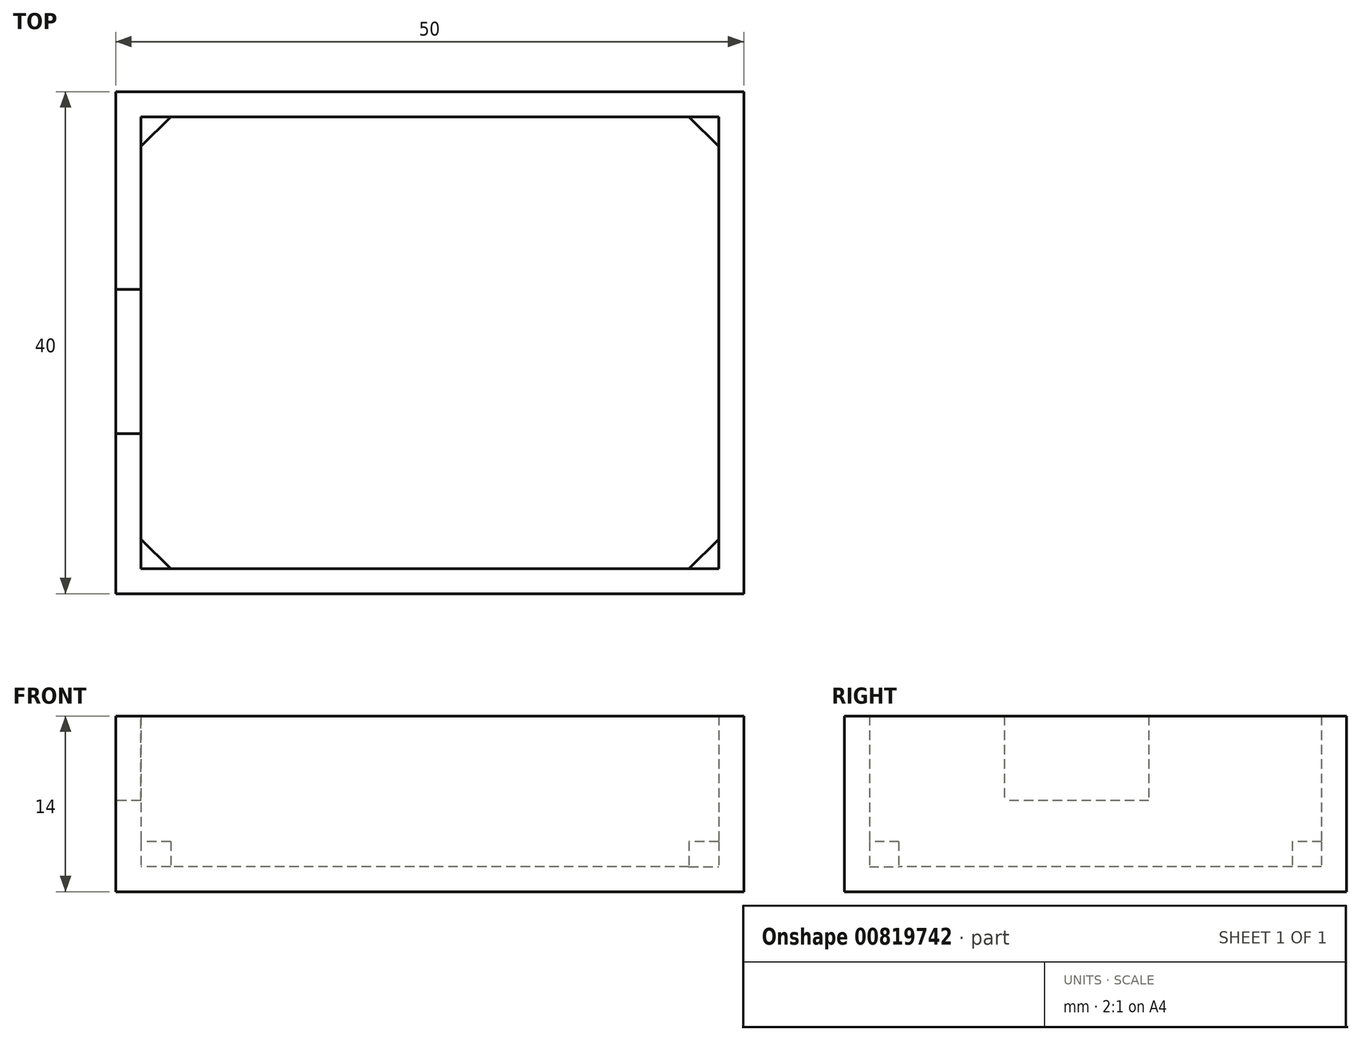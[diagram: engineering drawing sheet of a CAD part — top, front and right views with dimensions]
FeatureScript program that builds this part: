
annotation { "Feature Type Name" : "Feature", "Feature Type Description" : "" }
export const myFeature = defineFeature(function(context is Context, id is Id, definition is map)
    precondition{}
    {
        {
            var Q0;
            Q0=qCreatedBy(makeId("Top.planeOp"),FACE);
            var sketch = newSketch(context, id + "F0", { "sketchPlane" : qUnion([Q0])});
            skLineSegment(sketch, "E0.bottom", {"start": v(29.02, 30.23) * mm, "end": v(-16.98, 30.23) * mm});
            skLineSegment(sketch, "E0.top", {"start": v(29.02, -5.77) * mm, "end": v(-16.98, -5.77) * mm});
            skLineSegment(sketch, "E0.left", {"start": v(29.02, 30.23) * mm, "end": v(29.02, -5.77) * mm});
            skLineSegment(sketch, "E0.right", {"start": v(-16.98, 30.23) * mm, "end": v(-16.98, -5.77) * mm});
            skLineSegment(sketch, "E1.0", {"start": v(31.02, 32.23) * mm, "end": v(-18.98, 32.23) * mm});
            skLineSegment(sketch, "E1.1", {"start": v(31.02, 32.23) * mm, "end": v(31.02, -7.77) * mm});
            skLineSegment(sketch, "E1.2", {"start": v(31.02, -7.77) * mm, "end": v(-18.98, -7.77) * mm});
            skLineSegment(sketch, "E1.3", {"start": v(-18.98, 32.23) * mm, "end": v(-18.98, -7.77) * mm});
            skLineSegment(sketch, "E2", {"start": v(-14.6, 30.23) * mm, "end": v(-16.98, 27.88) * mm});
            skLineSegment(sketch, "E3", {"start": v(6.02, 32.23) * mm, "end": v(6.02, -7.77) * mm, "construction": true});
            skLineSegment(sketch, "E4", {"start": v(31.02, 12.23) * mm, "end": v(-18.98, 12.23) * mm, "construction": true});
            skLineSegment(sketch, "E5.MirrorCS", {"start": v(26.65, 30.23) * mm, "end": v(29.02, 27.88) * mm});
            skLineSegment(sketch, "E6.MirrorCS", {"start": v(26.65, -5.77) * mm, "end": v(29.02, -3.43) * mm});
            skLineSegment(sketch, "E7.MirrorCS", {"start": v(-14.6, -5.77) * mm, "end": v(-16.98, -3.43) * mm});
            skSolve(sketch);
        }
        {
            var Q0;
            {var subQ0=sQuery(id+"F0.wireOp",EDGE,"E2");Q0=makeQuery(id+"F0.imprint","IMPRINT",FACE,{"disambiguationData":[TD([[makeQuery(id+"F0.imprint","IMPRINT",EDGE,{"derivedFrom":subQ0}),1.0]])]});}
            extrude(context, id + "F1", {"entities" : qUnion([Q0]), "depth" : 2 * mm, "offsetDistance" : 25 * mm});
        }
        {
            var Q0;
            {var subQ3=sQuery(id+"F0.wireOp",EDGE,"E7.MirrorCS");Q0=makeQuery(id+"F0.imprint","IMPRINT",FACE,{"disambiguationData":[TD([[makeQuery(id+"F0.imprint","IMPRINT",EDGE,{"derivedFrom":subQ3}),1.0]])]});}
            var Q1;
            {var subQ3=sQuery(id+"F0.wireOp",EDGE,"E6.MirrorCS");Q1=makeQuery(id+"F0.imprint","IMPRINT",FACE,{"disambiguationData":[TD([[makeQuery(id+"F0.imprint","IMPRINT",EDGE,{"derivedFrom":subQ3}),-1.0]])]});}
            var Q2;
            {var subQ3=sQuery(id+"F0.wireOp",EDGE,"E2");Q2=makeQuery(id+"F0.imprint","IMPRINT",FACE,{"disambiguationData":[TD([[makeQuery(id+"F0.imprint","IMPRINT",EDGE,{"derivedFrom":subQ3}),-1.0]])]});}
            var Q3;
            {var subQ3=sQuery(id+"F0.wireOp",EDGE,"E5.MirrorCS");Q3=makeQuery(id+"F0.imprint","IMPRINT",FACE,{"disambiguationData":[TD([[makeQuery(id+"F0.imprint","IMPRINT",EDGE,{"derivedFrom":subQ3}),1.0]])]});}
            extrude(context, id + "F2", {"entities" : qUnion([Q0, Q1, Q2, Q3]), "operationType" : NewBodyOperationType.ADD, "depth" : 4 * mm, "offsetDistance" : 25 * mm});
        }
        {
            var Q0;
            Q0=makeQuery(id+"F0.imprint","IMPRINT",FACE,{"disambiguationData":[TD([[makeQuery(id+"F0.imprint","IMPRINT",EDGE,{"derivedFrom":sQuery(id+"F0.wireOp",EDGE,"E1.0")}),1.0]])]});
            extrude(context, id + "F3", {"entities" : qUnion([Q0]), "operationType" : NewBodyOperationType.ADD, "depth" : 14 * mm, "offsetDistance" : 25 * mm});
        }
        {
            var Q0;
            Q0=makeQuery(id+"F3.opExtrude","SWEPT_FACE",FACE,{"disambiguationData":[OSD([sQuery(id+"F0.wireOp",EDGE,"E1.3")])]});
            var sketch = newSketch(context, id + "F4", { "sketchPlane" : qUnion([Q0])});
            skLineSegment(sketch, "E8.bottom", {"start": v(-16.48, 15) * mm, "end": v(-4.98, 15) * mm});
            skLineSegment(sketch, "E8.top", {"start": v(-16.48, 7.25) * mm, "end": v(-4.98, 7.25) * mm});
            skLineSegment(sketch, "E8.left", {"start": v(-16.48, 15) * mm, "end": v(-16.48, 7.25) * mm});
            skLineSegment(sketch, "E8.right", {"start": v(-4.98, 15) * mm, "end": v(-4.98, 7.25) * mm});
            skSolve(sketch);
        }
        {
            var Q0;
            {var subQ0=sQuery(id+"F4.wireOp",EDGE,"E8.top");Q0=makeQuery(id+"F4.imprint","IMPRINT",FACE,{"disambiguationData":[TD([[makeQuery(id+"F4.imprint","IMPRINT",EDGE,{"derivedFrom":subQ0}),1.0]])]});}
            extrude(context, id + "F5", {"entities" : qUnion([Q0]), "operationType" : NewBodyOperationType.REMOVE, "oppositeDirection" : true, "depth" : 25 * mm, "offsetDistance" : 25 * mm});
        }
    });
